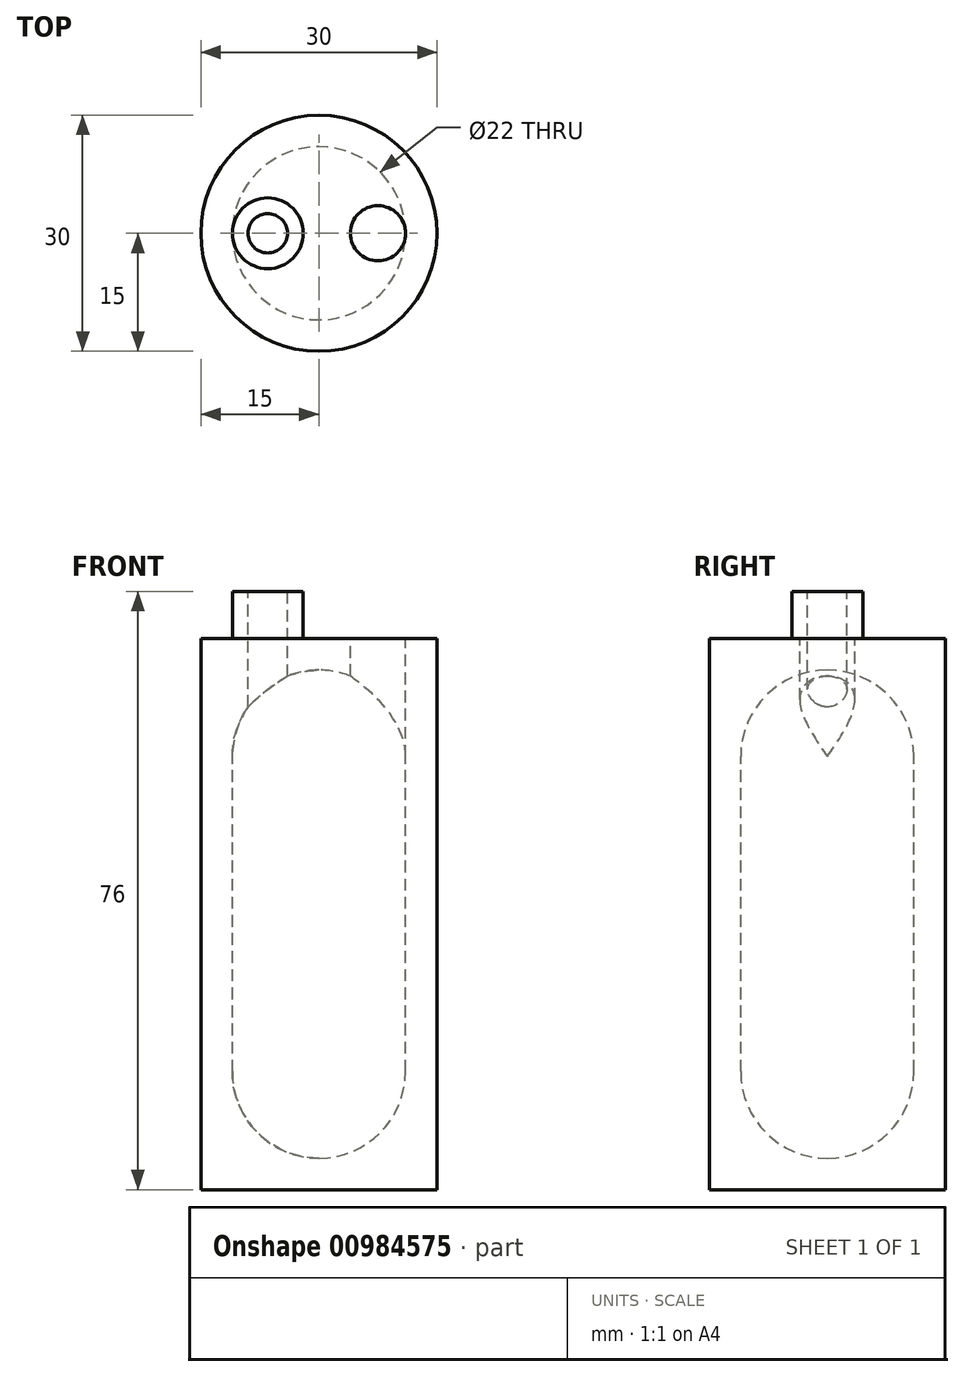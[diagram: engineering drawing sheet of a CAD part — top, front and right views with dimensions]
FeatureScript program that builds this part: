
annotation { "Feature Type Name" : "Feature", "Feature Type Description" : "" }
export const myFeature = defineFeature(function(context is Context, id is Id, definition is map)
    precondition{}
    {
        {
            var Q0;
            Q0=qCreatedBy(makeId("Front.planeOp"),FACE);
            var sketch = newSketch(context, id + "F0", { "sketchPlane" : qUnion([Q0])});
            skLineSegment(sketch, "E0.bottom", {"start": v(-15, 35) * mm, "end": v(15, 35) * mm});
            skLineSegment(sketch, "E0.top", {"start": v(-15, -35) * mm, "end": v(15, -35) * mm});
            skLineSegment(sketch, "E0.left", {"start": v(-15, 35) * mm, "end": v(-15, -35) * mm});
            skLineSegment(sketch, "E0.right", {"start": v(15, 35) * mm, "end": v(15, -35) * mm});
            skPoint(sketch, "E0.middle", {"position": v(0, 0) * mm});
            skLineSegment(sketch, "E1.bottom", {"start": v(-11, 20) * mm, "end": v(11, 20) * mm});
            skLineSegment(sketch, "E1.top", {"start": v(-11, -20) * mm, "end": v(11, -20) * mm});
            skLineSegment(sketch, "E1.left", {"start": v(-11, 20) * mm, "end": v(-11, -20) * mm});
            skLineSegment(sketch, "E1.right", {"start": v(11, 20) * mm, "end": v(11, -20) * mm});
            skCircle(sketch, "E2", {"center": v(0, 20) * mm, "radius": 11 * mm});
            skCircle(sketch, "E3", {"center": v(0, -20) * mm, "radius": 11 * mm});
            skLineSegment(sketch, "E4", {"start": v(0, 35) * mm, "end": v(0, -35) * mm});
            skSolve(sketch);
        }
        {
            var Q0;
            {var subQ0=sQuery(id+"F0.wireOp",EDGE,"E0.left");Q0=makeQuery(id+"F0.imprint","IMPRINT",FACE,{"disambiguationData":[TD([[makeQuery(id+"F0.imprint","IMPRINT",EDGE,{"derivedFrom":subQ0}),1.0]])]});}
            var Q1;
            Q1=sQuery(id+"F0.wireOp",EDGE,"E4");
            revolve(context, id + "F1", {"surfaceOperationType" : NewSurfaceOperationType.NEW, "entities" : qUnion([Q0]), "axis" : qUnion([Q1]), "revolveType" : RevolveType.FULL});
        }
        {
            var Q0;
            Q0=makeQuery(id+"F1.opRevolve","SWEPT_FACE",FACE,{"disambiguationData":[OSD([sQuery(id+"F0.wireOp",EDGE,"E0.bottom")])]});
            var sketch = newSketch(context, id + "F2", { "sketchPlane" : qUnion([Q0])});
            skCircle(sketch, "E5", {"center": v(-6.5, 0) * mm, "radius": 2.5 * mm});
            skCircle(sketch, "E6", {"center": v(-6.5, 0) * mm, "radius": 4.5 * mm});
            skCircle(sketch, "E7", {"center": v(7.5, 0) * mm, "radius": 3.5 * mm});
            skSolve(sketch);
        }
        {
            var Q0;
            Q0=makeQuery(id+"F2.imprint","IMPRINT",FACE,{"disambiguationData":[TD([[makeQuery(id+"F2.imprint","IMPRINT",EDGE,{"derivedFrom":sQuery(id+"F2.wireOp",EDGE,"E7")}),1.0]])]});
            var Q1;
            Q1=makeQuery(id+"F2.imprint","IMPRINT",FACE,{"disambiguationData":[TD([[makeQuery(id+"F2.imprint","IMPRINT",EDGE,{"derivedFrom":sQuery(id+"F2.wireOp",EDGE,"E5")}),1.0]])]});
            extrude(context, id + "F3", {"entities" : qUnion([Q0, Q1]), "operationType" : NewBodyOperationType.REMOVE, "oppositeDirection" : true, "depth" : 25 * mm, "offsetDistance" : 25 * mm});
        }
        {
            var Q0;
            Q0=makeQuery(id+"F2.imprint","IMPRINT",FACE,{"disambiguationData":[TD([[makeQuery(id+"F2.imprint","IMPRINT",EDGE,{"derivedFrom":sQuery(id+"F2.wireOp",EDGE,"E5")}),-1.0]])]});
            extrude(context, id + "F4", {"entities" : qUnion([Q0]), "operationType" : NewBodyOperationType.ADD, "depth" : 6 * mm, "offsetDistance" : 25 * mm});
        }
    });
